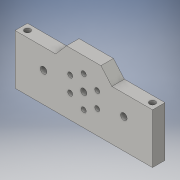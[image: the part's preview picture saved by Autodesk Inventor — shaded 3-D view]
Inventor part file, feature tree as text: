
AUTODESK INVENTOR PART (.ipt)
format: ipt  version: 2016 (Build 200138000, 138)  size: 375,808 bytes
history: native  units: mm
features: projected_geometry x8, extrude x5, other x4, sketch x3, fillet x2, hole x1
ambient origin geometry x8: Origin, YZ Plane, XZ Plane, XY Plane, X Axis, Y Axis, Z Axis, Center Point
bodies: Body1 (feature_tree)
feature tree (23):
  other  "構築線"
  extrude  "押し出し11"  Depth=17.0mm
  other  "固定穴"
  extrude  "押し出し19"  Depth=5.6mm
  extrude  "押し出し21"  Depth=10.0mm
  other  "ねじ穴+固定(基板)"
  hole  "ねじ穴(基板)"  [1 undecoded]
  extrude  "押し出し22"  Depth=10.0mm
  fillet  "フィレット1"  [1 undecoded]
  fillet  "フィレット2"  Radius=20.1mm
  extrude  "押し出し28"  TaperAngle=0.0deg  [1 undecoded]
  other  "外形上面(dxf出力用)"
  sketch  "スケッチ25"
  sketch  "スケッチ27"
  sketch  "スケッチ20"
  projected_geometry  "投影ループ4"
  projected_geometry  "投影ループ5"
  projected_geometry  "投影ループ6"
  projected_geometry  "投影ループ7"
  projected_geometry  "投影ループ8"
  projected_geometry  "投影ループ13"
  projected_geometry  "投影ループ14"
  projected_geometry  "投影ループ16"
note: 3 required parameter values undecoded (feature->parameter linkage not recoverable at this tier; creation-order binding heuristic only, values carry confidence <= 0.55)
